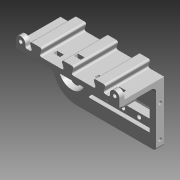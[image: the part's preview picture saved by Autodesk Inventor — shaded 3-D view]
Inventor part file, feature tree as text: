
AUTODESK INVENTOR PART (.ipt)
format: ipt  version: 2015 (Build 190159000, 159)  size: 299,520 bytes
history: native  units: mm (DEFAULTED — no unit token found)
features: other x11, fillet x1
bodies: Body1 (feature_tree)
feature tree (12):
  other  "combined_base_caterpillar_narrow_A.iam"
  other  "support_caterpillar_top_v3_narrow.ipt:1"
  other  "support_caterpillar_lateral_v3_Left.ipt:1"
  other  "Sólido1"
  other  "Origen"
  fillet  "Empalme1"  Radius=10.0mm
  other  "Plano YZ"
  other  "Plano XZ"
  other  "Plano XY"
  other  "Eje X"
  other  "Eje Y"
  other  "Eje Z"
